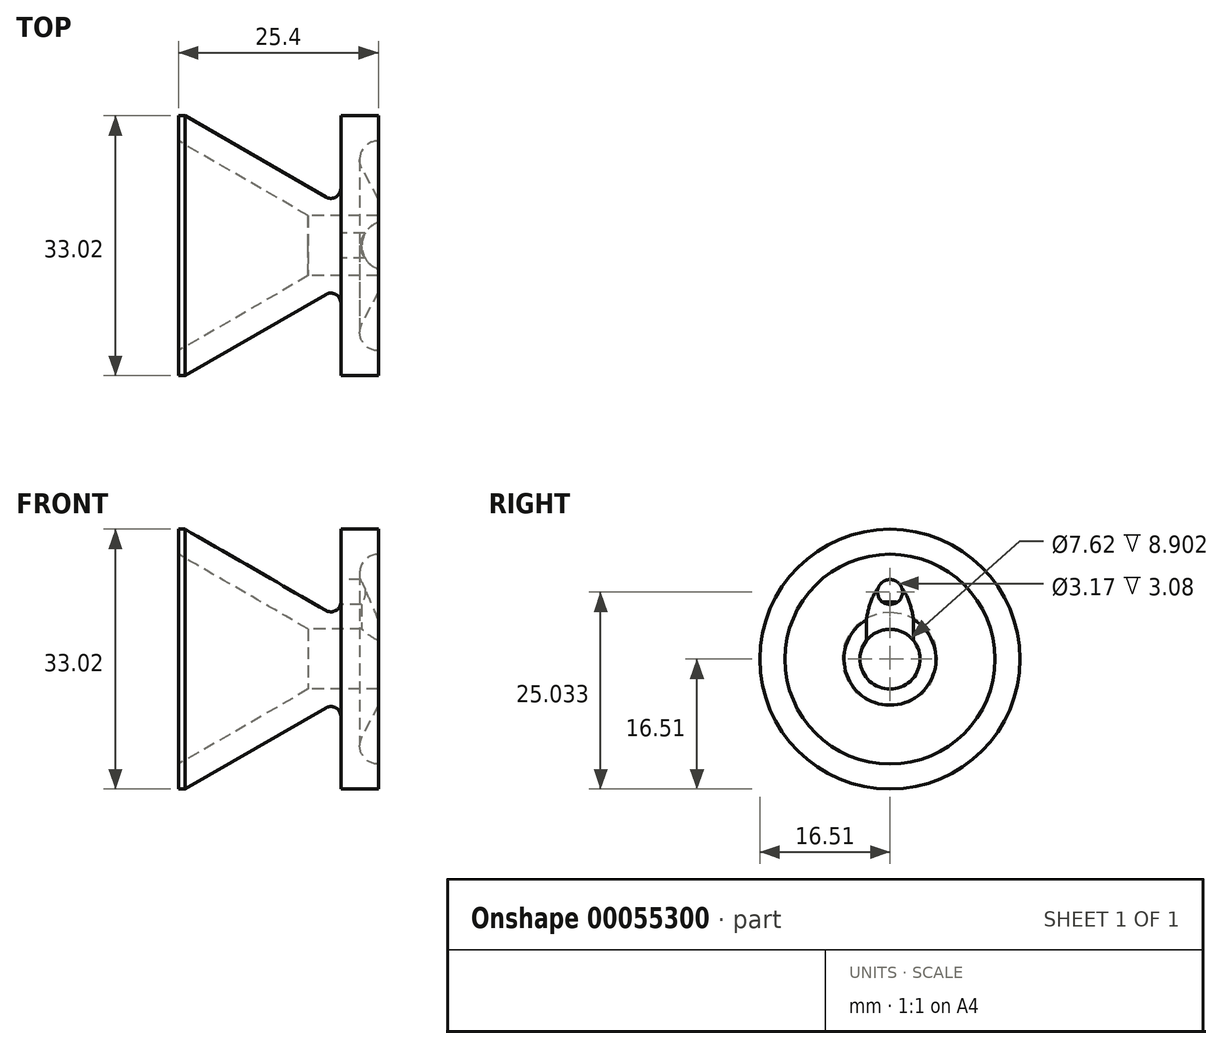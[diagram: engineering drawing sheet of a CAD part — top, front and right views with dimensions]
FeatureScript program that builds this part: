
annotation { "Feature Type Name" : "Feature", "Feature Type Description" : "" }
export const myFeature = defineFeature(function(context is Context, id is Id, definition is map)
    precondition{}
    {
        {
            var Q0;
            Q0=qCreatedBy(makeId("Front.planeOp"),FACE);
            var sketch = newSketch(context, id + "F0", { "sketchPlane" : qUnion([Q0])});
            skLineSegment(sketch, "E0", {"start": v(-20.64, 16.51) * mm, "end": v(-19.79, 16.51) * mm});
            skLineSegment(sketch, "E1", {"start": v(-19.79, 16.51) * mm, "end": v(-1.9, 6.19) * mm});
            skLineSegment(sketch, "E2", {"start": v(0, 7.29) * mm, "end": v(0, 16.51) * mm});
            skLineSegment(sketch, "E3", {"start": v(0, 16.51) * mm, "end": v(4.76, 16.51) * mm});
            skLineSegment(sketch, "E4", {"start": v(4.76, 13.34) * mm, "end": v(4.76, 16.51) * mm});
            skLineSegment(sketch, "E5", {"start": v(-20.64, 16.51) * mm, "end": v(-20.64, 13.34) * mm});
            skLineSegment(sketch, "E6", {"start": v(-20.64, 13.34) * mm, "end": v(-4.14, 3.81) * mm});
            skLineSegment(sketch, "E7", {"start": v(-4.14, 3.81) * mm, "end": v(4.76, 3.81) * mm});
            skLineSegment(sketch, "E8", {"start": v(-22.8, 0) * mm, "end": v(16.35, 0) * mm, "construction": true});
            skLineSegment(sketch, "E9", {"start": v(4.76, 13.34) * mm, "end": v(0, 13.34) * mm, "construction": true});
            skPoint(sketch, "E10.visualSharp", {"position": v(0, 5.09) * mm});
            skArc(sketch, "E10.filletArc", {"start": v(-1.9, 6.19) * mm, "mid": v(-0.64, 6.19) * mm, "end": v(0, 7.29) * mm});
            skLineSegment(sketch, "E11", {"start": v(4.76, 3.81) * mm, "end": v(4.76, 5.84) * mm});
            skArc(sketch, "E12", {"start": v(4.76, 13.34) * mm, "mid": v(2.72, 12.18) * mm, "end": v(2.66, 9.84) * mm});
            skLineSegment(sketch, "E13", {"start": v(4.76, 5.84) * mm, "end": v(2.66, 9.84) * mm});
            skSolve(sketch);
        }
        {
            var Q0;
            Q0 = qSketchRegion(id + "F0", true);
            var Q1;
            Q1=sQuery(id+"F0.wireOp",EDGE,"E8");
            revolve(context, id + "F1", {"entities" : qUnion([Q0]), "axis" : qUnion([Q1]), "revolveType" : RevolveType.FULL});
        }
        {
            var Q0;
            Q0=makeQuery(id+"F1.opRevolve","SWEPT_BODY",BODY,{"disambiguationData":[OSD([sQuery(id+"F0.wireOp",EDGE,"E0"),sQuery(id+"F0.wireOp",EDGE,"E1"),sQuery(id+"F0.wireOp",EDGE,"E2"),sQuery(id+"F0.wireOp",EDGE,"E3"),sQuery(id+"F0.wireOp",EDGE,"E4"),sQuery(id+"F0.wireOp",EDGE,"E5"),sQuery(id+"F0.wireOp",EDGE,"E6"),sQuery(id+"F0.wireOp",EDGE,"E7"),sQuery(id+"F0.wireOp",EDGE,"E10.filletArc"),sQuery(id+"F0.wireOp",EDGE,"E11"),sQuery(id+"F0.wireOp",EDGE,"E12"),sQuery(id+"F0.wireOp",EDGE,"E13")])]});
            transform(context, id + "F2", {"entities" : qUnion([Q0]), "transformType" : TransformType.TRANSLATION_3D, "dx" : 0 * mm, "dy" : 0 * mm, "dz" : 0 * mm, "makeCopy" : true});
        }
        {
            var Q0;
            Q0=makeQuery(id+"F2.opPattern","COPY",BODY,{"derivedFrom":makeQuery(id+"F1.opRevolve","SWEPT_BODY",BODY,{"disambiguationData":[OSD([sQuery(id+"F0.wireOp",EDGE,"E0"),sQuery(id+"F0.wireOp",EDGE,"E1"),sQuery(id+"F0.wireOp",EDGE,"E2"),sQuery(id+"F0.wireOp",EDGE,"E3"),sQuery(id+"F0.wireOp",EDGE,"E4"),sQuery(id+"F0.wireOp",EDGE,"E5"),sQuery(id+"F0.wireOp",EDGE,"E6"),sQuery(id+"F0.wireOp",EDGE,"E7"),sQuery(id+"F0.wireOp",EDGE,"E10.filletArc"),sQuery(id+"F0.wireOp",EDGE,"E11"),sQuery(id+"F0.wireOp",EDGE,"E12"),sQuery(id+"F0.wireOp",EDGE,"E13")])]}),"instanceName":"1"});
            deleteBodies(context, id + "F3", {"entities" : qUnion([Q0])});
        }
        {
            var Q0;
            Q0=qCreatedBy(makeId("Top.planeOp"),FACE);
            var sketch = newSketch(context, id + "F4", { "sketchPlane" : qUnion([Q0])});
            skCircle(sketch, "E14", {"center": v(5.83, 0) * mm, "radius": 3.18 * mm});
            skSolve(sketch);
        }
        {
            var Q0;
            Q0 = qSketchRegion(id + "F4", true);
            extrude(context, id + "F5", {"entities" : qUnion([Q0]), "operationType" : NewBodyOperationType.REMOVE, "depth" : 10.16 * mm});
        }
        {
            var Q0;
            Q0=qCreatedBy(makeId("Right.planeOp"),FACE);
            var sketch = newSketch(context, id + "F6", { "sketchPlane" : qUnion([Q0])});
            skPoint(sketch, "E15", {"position": v(0, 8.52) * mm});
            skSolve(sketch);
        }
        {
            var Q0;
            Q0=sQuery(id+"F6.wireOp",VERTEX,"E15");
            var Q1;
            Q1=makeQuery(id+"F1.opRevolve","SWEPT_BODY",BODY,{"disambiguationData":[OSD([sQuery(id+"F0.wireOp",EDGE,"E0"),sQuery(id+"F0.wireOp",EDGE,"E1"),sQuery(id+"F0.wireOp",EDGE,"E2"),sQuery(id+"F0.wireOp",EDGE,"E3"),sQuery(id+"F0.wireOp",EDGE,"E4"),sQuery(id+"F0.wireOp",EDGE,"E5"),sQuery(id+"F0.wireOp",EDGE,"E6"),sQuery(id+"F0.wireOp",EDGE,"E7"),sQuery(id+"F0.wireOp",EDGE,"E10.filletArc"),sQuery(id+"F0.wireOp",EDGE,"E11"),sQuery(id+"F0.wireOp",EDGE,"E12"),sQuery(id+"F0.wireOp",EDGE,"E13")])]});
            hole(context, id + "F7", {"style" : HoleStyle.SIMPLE, "holeDiameter" : 3.17 * mm, "endStyle" : HoleEndStyle.THROUGH, "oppositeDirection" : true, "locations" : qUnion([Q0]), "scope" : qUnion([Q1])});
        }
    });
